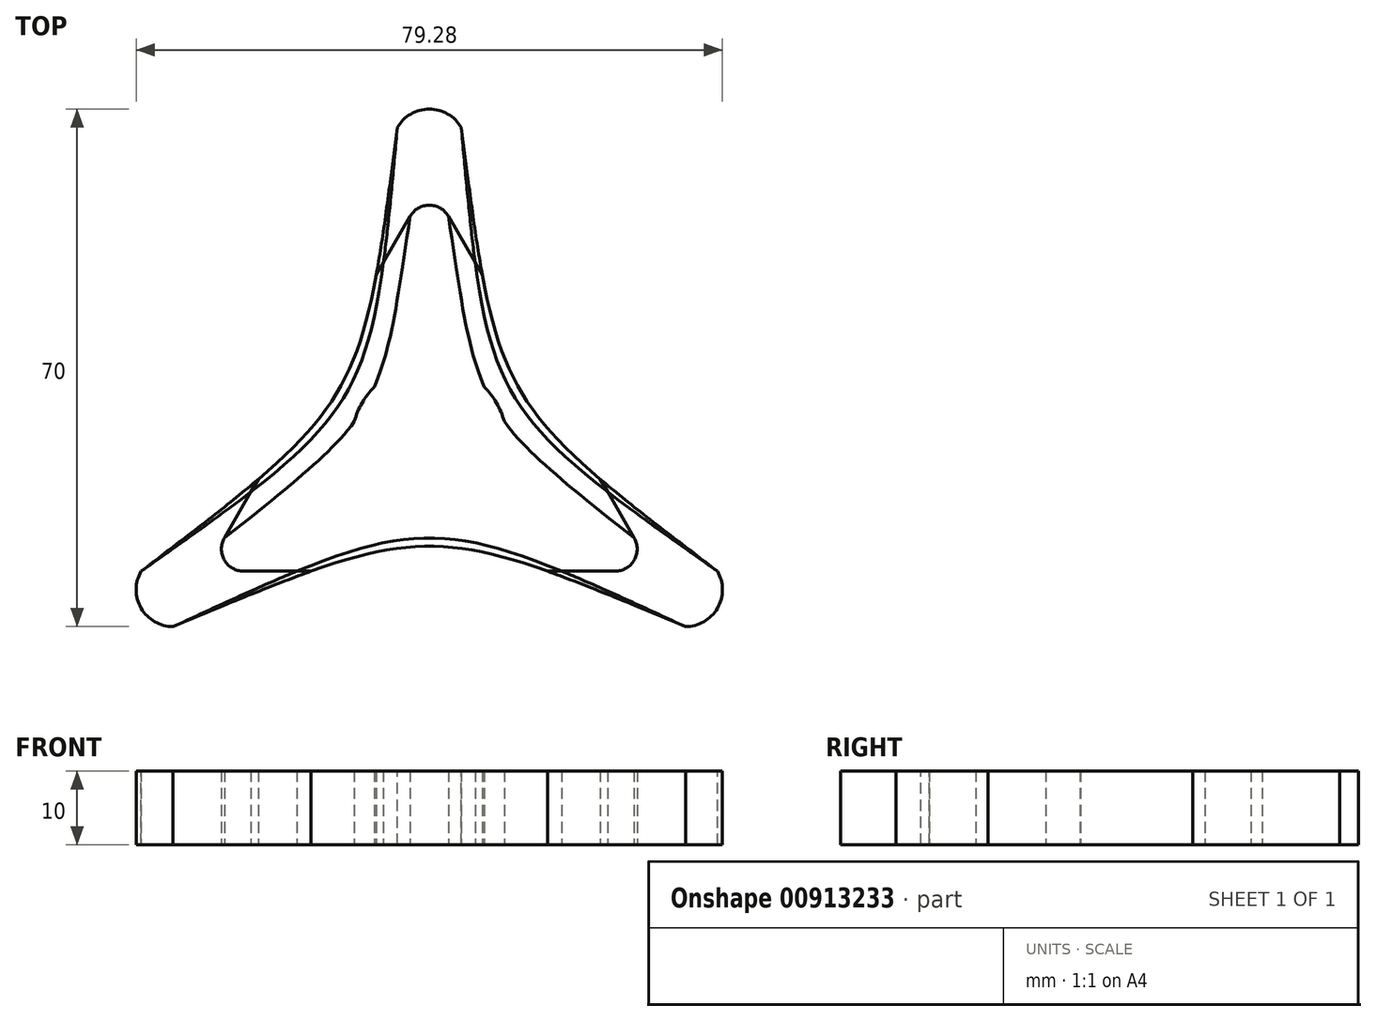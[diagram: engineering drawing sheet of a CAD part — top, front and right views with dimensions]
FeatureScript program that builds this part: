
annotation { "Feature Type Name" : "Feature", "Feature Type Description" : "" }
export const myFeature = defineFeature(function(context is Context, id is Id, definition is map)
    precondition{}
    {
        {
            var Q0;
            Q0=qCreatedBy(makeId("Top.planeOp"),FACE);
            var sketch = newSketch(context, id + "F0", { "sketchPlane" : qUnion([Q0])});
            skCircle(sketch, "E0", {"center": v(0, 0) * mm, "radius": 10.5 * mm});
            skCircle(sketch, "E1", {"center": v(0, 0) * mm, "radius": 50 * mm});
            skCircle(sketch, "E2", {"center": v(0, 0) * mm, "radius": 35 * mm});
            skCircle(sketch, "E3", {"center": v(0, 0) * mm, "radius": 7.5 * mm});
            skCircle(sketch, "E4.cCircle", {"center": v(0, 0) * mm, "radius": 7.5 * mm, "construction": true});
            skLineSegment(sketch, "E4.0", {"start": v(0, -7.5) * mm, "end": v(-6.5, 3.75) * mm});
            skLineSegment(sketch, "E4.1", {"start": v(-6.5, 3.75) * mm, "end": v(6.5, 3.75) * mm});
            skLineSegment(sketch, "E4.2", {"start": v(6.5, 3.75) * mm, "end": v(0, -7.5) * mm});
            skCircle(sketch, "E5.cCircle", {"center": v(0, 0) * mm, "radius": 10.5 * mm, "construction": true});
            skLineSegment(sketch, "E5.0", {"start": v(0, -10.5) * mm, "end": v(-9.1, 5.25) * mm});
            skLineSegment(sketch, "E5.1", {"start": v(-9.1, 5.25) * mm, "end": v(9.1, 5.25) * mm});
            skLineSegment(sketch, "E5.2", {"start": v(9.1, 5.25) * mm, "end": v(0, -10.5) * mm});
            skCircle(sketch, "E6.cCircle", {"center": v(0, 0) * mm, "radius": 35 * mm, "construction": true});
            skLineSegment(sketch, "E6.0", {"start": v(2.6, 30.5) * mm, "end": v(27.71, -13) * mm});
            skLineSegment(sketch, "E6.1", {"start": v(25.11, -17.5) * mm, "end": v(-25.11, -17.5) * mm});
            skLineSegment(sketch, "E6.2", {"start": v(-27.71, -13) * mm, "end": v(-2.6, 30.5) * mm});
            skCircle(sketch, "E7.cCircle", {"center": v(0, 0) * mm, "radius": 50 * mm, "construction": true});
            skLineSegment(sketch, "E7.0", {"start": v(4.33, 42.5) * mm, "end": v(38.97, -17.5) * mm});
            skLineSegment(sketch, "E7.1", {"start": v(34.64, -25) * mm, "end": v(-34.64, -25) * mm});
            skLineSegment(sketch, "E7.2", {"start": v(-38.97, -17.5) * mm, "end": v(-4.33, 42.5) * mm});
            skPoint(sketch, "E8.visualSharp", {"position": v(0, 50) * mm});
            skArc(sketch, "E8.filletArc", {"start": v(4.33, 42.5) * mm, "mid": v(0, 45) * mm, "end": v(-4.33, 42.5) * mm});
            skPoint(sketch, "E9.visualSharp", {"position": v(43.3, -25) * mm});
            skArc(sketch, "E9.filletArc", {"start": v(34.64, -25) * mm, "mid": v(38.97, -22.5) * mm, "end": v(38.97, -17.5) * mm});
            skPoint(sketch, "E10.visualSharp", {"position": v(-43.3, -25) * mm});
            skArc(sketch, "E10.filletArc", {"start": v(-38.97, -17.5) * mm, "mid": v(-38.97, -22.5) * mm, "end": v(-34.64, -25) * mm});
            skPoint(sketch, "E11.visualSharp", {"position": v(0, 35) * mm});
            skArc(sketch, "E11.filletArc", {"start": v(2.6, 30.5) * mm, "mid": v(0, 32) * mm, "end": v(-2.6, 30.5) * mm});
            skPoint(sketch, "E12.visualSharp", {"position": v(30.31, -17.5) * mm});
            skArc(sketch, "E12.filletArc", {"start": v(25.11, -17.5) * mm, "mid": v(27.71, -16) * mm, "end": v(27.71, -13) * mm});
            skPoint(sketch, "E13.visualSharp", {"position": v(-30.31, -17.5) * mm});
            skArc(sketch, "E13.filletArc", {"start": v(-27.71, -13) * mm, "mid": v(-27.71, -16) * mm, "end": v(-25.11, -17.5) * mm});
            skFitSpline(sketch, "E14", {"points": [v(4.33, 42.5) * mm, v(38.97, -17.5) * mm], "startDerivative": vector(14.29, -111.75) * mm, "endDerivative": vector(89.63, -68.25) * mm});
            skFitSpline(sketch, "E15", {"points": [v(27.71, -13) * mm, v(2.6, 30.5) * mm], "startDerivative": vector(-63.65, 50.25) * mm, "endDerivative": vector(-11.7, 80.25) * mm});
            skFitSpline(sketch, "E16", {"points": [v(-2.6, 30.5) * mm, v(-27.71, -13) * mm], "startDerivative": vector(-11.7, -80.25) * mm, "endDerivative": vector(-63.65, -50.25) * mm});
            skFitSpline(sketch, "E17", {"points": [v(-4.33, 42.5) * mm, v(-38.97, -17.5) * mm], "startDerivative": vector(-14.29, -111.75) * mm, "endDerivative": vector(-89.63, -68.25) * mm});
            skFitSpline(sketch, "E18", {"points": [v(-25.11, -17.5) * mm, v(25.11, -17.5) * mm], "startDerivative": vector(75.34, 30) * mm, "endDerivative": vector(75.34, -30) * mm});
            skFitSpline(sketch, "E19", {"points": [v(34.64, -25) * mm, v(-34.64, -25) * mm], "startDerivative": vector(-103.92, 43.5) * mm, "endDerivative": vector(-103.92, -43.5) * mm});
            skCircle(sketch, "E20", {"center": v(0, 0) * mm, "radius": 9 * mm});
            skLineSegment(sketch, "E21", {"start": v(-25.11, -17.5) * mm, "end": v(25.11, -17.5) * mm});
            skFitSpline(sketch, "E22", {"points": [v(-34.64, -25) * mm, v(34.64, -25) * mm], "startDerivative": vector(103.92, 48) * mm, "endDerivative": vector(103.92, -48) * mm});
            skFitSpline(sketch, "E23", {"points": [v(4.33, 42.5) * mm, v(38.97, -17.5) * mm], "startDerivative": vector(10.4, -114) * mm, "endDerivative": vector(93.53, -66) * mm});
            skFitSpline(sketch, "E24", {"points": [v(-4.33, 42.5) * mm, v(-38.97, -17.5) * mm], "startDerivative": vector(-10.4, -114) * mm, "endDerivative": vector(-93.53, -66) * mm});
            skCircle(sketch, "E25.cCircle", {"center": v(0, 0) * mm, "radius": 9 * mm, "construction": true});
            skLineSegment(sketch, "E25.0", {"start": v(0, -9) * mm, "end": v(-7.8, 4.5) * mm});
            skLineSegment(sketch, "E25.1", {"start": v(-7.8, 4.5) * mm, "end": v(7.8, 4.5) * mm});
            skLineSegment(sketch, "E25.2", {"start": v(7.8, 4.5) * mm, "end": v(0, -9) * mm});
            skSolve(sketch);
        }
        {
            var Q0;
            {var subQ1=sQuery(id+"F0.wireOp",EDGE,"E6.1");var subQ3=sQuery(id+"F0.wireOp",EDGE,"E19");var subQ6=makeQuery(id+"F0.imprint","INTERSECT",VERTEX,{"disambiguationData":[OD(0.0)],"derivedFrom":[subQ1,subQ3]});Q0=makeQuery(id+"F0.imprint","IMPRINT",FACE,{"disambiguationData":[TD([[makeQuery(id+"F0.imprint","IMPRINT",EDGE,{"disambiguationData":[TD([[subQ6,-1.0]])],"derivedFrom":subQ3}),-1.0]])]});}
            var Q1;
            {var subQ0=sQuery(id+"F0.wireOp",EDGE,"E12.filletArc");Q1=makeQuery(id+"F0.imprint","IMPRINT",FACE,{"disambiguationData":[TD([[makeQuery(id+"F0.imprint","IMPRINT",EDGE,{"derivedFrom":subQ0}),-1.0]])]});}
            var Q2;
            {var subQ5=sQuery(id+"F0.wireOp",EDGE,"E9.filletArc");Q2=makeQuery(id+"F0.imprint","IMPRINT",FACE,{"disambiguationData":[TD([[makeQuery(id+"F0.imprint","IMPRINT",EDGE,{"derivedFrom":subQ5}),1.0]])]});}
            var Q3;
            {var subQ1=sQuery(id+"F0.wireOp",EDGE,"E6.0");var subQ3=sQuery(id+"F0.wireOp",EDGE,"E14");var subQ4=makeQuery(id+"F0.imprint","INTERSECT",VERTEX,{"disambiguationData":[OD(0.0)],"derivedFrom":[subQ1,subQ3]});Q3=makeQuery(id+"F0.imprint","IMPRINT",FACE,{"disambiguationData":[TD([[makeQuery(id+"F0.imprint","IMPRINT",EDGE,{"disambiguationData":[TD([[subQ4,-1.0]])],"derivedFrom":subQ3}),-1.0]])]});}
            var Q4;
            {var subQ0=sQuery(id+"F0.wireOp",EDGE,"E13.filletArc");Q4=makeQuery(id+"F0.imprint","IMPRINT",FACE,{"disambiguationData":[TD([[makeQuery(id+"F0.imprint","IMPRINT",EDGE,{"derivedFrom":subQ0}),-1.0]])]});}
            var Q5;
            {var subQ5=sQuery(id+"F0.wireOp",EDGE,"E10.filletArc");Q5=makeQuery(id+"F0.imprint","IMPRINT",FACE,{"disambiguationData":[TD([[makeQuery(id+"F0.imprint","IMPRINT",EDGE,{"derivedFrom":subQ5}),1.0]])]});}
            var Q6;
            {var subQ1=sQuery(id+"F0.wireOp",EDGE,"E6.2");var subQ3=sQuery(id+"F0.wireOp",EDGE,"E17");var subQ5=makeQuery(id+"F0.imprint","INTERSECT",VERTEX,{"disambiguationData":[OD(0.0)],"derivedFrom":[subQ1,subQ3]});Q6=makeQuery(id+"F0.imprint","IMPRINT",FACE,{"disambiguationData":[TD([[makeQuery(id+"F0.imprint","IMPRINT",EDGE,{"disambiguationData":[TD([[subQ5,1.0]])],"derivedFrom":subQ3}),1.0]])]});}
            var Q7;
            {var subQ5=sQuery(id+"F0.wireOp",EDGE,"E8.filletArc");Q7=makeQuery(id+"F0.imprint","IMPRINT",FACE,{"disambiguationData":[TD([[makeQuery(id+"F0.imprint","IMPRINT",EDGE,{"derivedFrom":subQ5}),1.0]])]});}
            var Q8;
            {var subQ0=sQuery(id+"F0.wireOp",EDGE,"E11.filletArc");Q8=makeQuery(id+"F0.imprint","IMPRINT",FACE,{"disambiguationData":[TD([[makeQuery(id+"F0.imprint","IMPRINT",EDGE,{"derivedFrom":subQ0}),-1.0]])]});}
            extrude(context, id + "F1", {"entities" : qUnion([Q0, Q1, Q2, Q3, Q4, Q5, Q6, Q7, Q8]), "depth" : 10 * mm, "offsetDistance" : 25 * mm});
        }
        {
            var Q0;
            {var subQ5=sQuery(id+"F0.wireOp",EDGE,"E10.filletArc");Q0=makeQuery(id+"F0.imprint","IMPRINT",FACE,{"disambiguationData":[TD([[makeQuery(id+"F0.imprint","IMPRINT",EDGE,{"derivedFrom":subQ5}),1.0]])]});}
            var Q1;
            {var subQ1=sQuery(id+"F0.wireOp",EDGE,"E13.filletArc");Q1=makeQuery(id+"F0.imprint","IMPRINT",FACE,{"disambiguationData":[TD([[makeQuery(id+"F0.imprint","IMPRINT",EDGE,{"derivedFrom":subQ1}),-1.0]])]});}
            var Q2;
            {var subQ0=sQuery(id+"F0.wireOp",EDGE,"E21");var subQ8=sQuery(id+"F0.wireOp",EDGE,"E22");var subQ9=makeQuery(id+"F0.imprint","INTERSECT",VERTEX,{"disambiguationData":[OD(0.0)],"derivedFrom":[subQ0,subQ8]});Q2=makeQuery(id+"F0.imprint","IMPRINT",FACE,{"disambiguationData":[TD([[makeQuery(id+"F0.imprint","IMPRINT",EDGE,{"disambiguationData":[TD([[subQ9,-1.0]])],"derivedFrom":subQ8}),1.0]])]});}
            var Q3;
            {var subQ1=sQuery(id+"F0.wireOp",EDGE,"E6.2");var subQ3=sQuery(id+"F0.wireOp",EDGE,"E24");var subQ6=makeQuery(id+"F0.imprint","INTERSECT",VERTEX,{"disambiguationData":[OD(0.0)],"derivedFrom":[subQ1,subQ3]});Q3=makeQuery(id+"F0.imprint","IMPRINT",FACE,{"disambiguationData":[TD([[makeQuery(id+"F0.imprint","IMPRINT",EDGE,{"disambiguationData":[TD([[subQ6,1.0]])],"derivedFrom":subQ3}),1.0]])]});}
            var Q4;
            {var subQ0=sQuery(id+"F0.wireOp",EDGE,"E17");var subQ1=sQuery(id+"F0.wireOp",EDGE,"E2");var subQ2=makeQuery(id+"F0.imprint","INTERSECT",VERTEX,{"disambiguationData":[OD(1.0)],"derivedFrom":[subQ1,subQ0]});Q4=makeQuery(id+"F0.imprint","IMPRINT",FACE,{"disambiguationData":[TD([[makeQuery(id+"F0.imprint","IMPRINT",EDGE,{"disambiguationData":[TD([[subQ2,-1.0]])],"derivedFrom":subQ1}),1.0]])]});}
            var Q5;
            {var subQ0=sQuery(id+"F0.wireOp",EDGE,"E17");var subQ1=sQuery(id+"F0.wireOp",EDGE,"E2");var subQ2=makeQuery(id+"F0.imprint","INTERSECT",VERTEX,{"disambiguationData":[OD(1.0)],"derivedFrom":[subQ1,subQ0]});Q5=makeQuery(id+"F0.imprint","IMPRINT",FACE,{"disambiguationData":[TD([[makeQuery(id+"F0.imprint","IMPRINT",EDGE,{"disambiguationData":[TD([[subQ2,-1.0]])],"derivedFrom":subQ1}),-1.0]])]});}
            var Q6;
            {var subQ0=sQuery(id+"F0.wireOp",EDGE,"E22");var subQ1=sQuery(id+"F0.wireOp",EDGE,"E2");var subQ2=makeQuery(id+"F0.imprint","INTERSECT",VERTEX,{"disambiguationData":[OD(0.0)],"derivedFrom":[subQ1,subQ0]});Q6=makeQuery(id+"F0.imprint","IMPRINT",FACE,{"disambiguationData":[TD([[makeQuery(id+"F0.imprint","IMPRINT",EDGE,{"disambiguationData":[TD([[subQ2,-1.0]])],"derivedFrom":subQ1}),-1.0]])]});}
            var Q7;
            {var subQ0=sQuery(id+"F0.wireOp",EDGE,"E22");var subQ1=sQuery(id+"F0.wireOp",EDGE,"E2");var subQ2=makeQuery(id+"F0.imprint","INTERSECT",VERTEX,{"disambiguationData":[OD(0.0)],"derivedFrom":[subQ1,subQ0]});Q7=makeQuery(id+"F0.imprint","IMPRINT",FACE,{"disambiguationData":[TD([[makeQuery(id+"F0.imprint","IMPRINT",EDGE,{"disambiguationData":[TD([[subQ2,-1.0]])],"derivedFrom":subQ1}),1.0]])]});}
            var Q8;
            {var subQ0=sQuery(id+"F0.wireOp",EDGE,"E21");var subQ1=sQuery(id+"F0.wireOp",EDGE,"E19");var subQ2=makeQuery(id+"F0.imprint","INTERSECT",VERTEX,{"disambiguationData":[OD(0.0)],"derivedFrom":[subQ1,subQ0]});Q8=makeQuery(id+"F0.imprint","IMPRINT",FACE,{"disambiguationData":[TD([[makeQuery(id+"F0.imprint","IMPRINT",EDGE,{"disambiguationData":[TD([[subQ2,-1.0]])],"derivedFrom":subQ1}),-1.0]])]});}
            var Q9;
            {var subQ1=sQuery(id+"F0.wireOp",EDGE,"E12.filletArc");Q9=makeQuery(id+"F0.imprint","IMPRINT",FACE,{"disambiguationData":[TD([[makeQuery(id+"F0.imprint","IMPRINT",EDGE,{"derivedFrom":subQ1}),-1.0]])]});}
            var Q10;
            {var subQ1=sQuery(id+"F0.wireOp",EDGE,"E6.0");var subQ3=sQuery(id+"F0.wireOp",EDGE,"E23");var subQ4=makeQuery(id+"F0.imprint","INTERSECT",VERTEX,{"disambiguationData":[OD(0.0)],"derivedFrom":[subQ1,subQ3]});Q10=makeQuery(id+"F0.imprint","IMPRINT",FACE,{"disambiguationData":[TD([[makeQuery(id+"F0.imprint","IMPRINT",EDGE,{"disambiguationData":[TD([[subQ4,-1.0]])],"derivedFrom":subQ3}),-1.0]])]});}
            var Q11;
            {var subQ5=sQuery(id+"F0.wireOp",EDGE,"E9.filletArc");Q11=makeQuery(id+"F0.imprint","IMPRINT",FACE,{"disambiguationData":[TD([[makeQuery(id+"F0.imprint","IMPRINT",EDGE,{"derivedFrom":subQ5}),1.0]])]});}
            var Q12;
            {var subQ0=sQuery(id+"F0.wireOp",EDGE,"E19");var subQ1=sQuery(id+"F0.wireOp",EDGE,"E2");var subQ2=makeQuery(id+"F0.imprint","INTERSECT",VERTEX,{"disambiguationData":[OD(1.0)],"derivedFrom":[subQ1,subQ0]});Q12=makeQuery(id+"F0.imprint","IMPRINT",FACE,{"disambiguationData":[TD([[makeQuery(id+"F0.imprint","IMPRINT",EDGE,{"disambiguationData":[TD([[subQ2,-1.0]])],"derivedFrom":subQ1}),-1.0]])]});}
            var Q13;
            {var subQ0=sQuery(id+"F0.wireOp",EDGE,"E19");var subQ1=sQuery(id+"F0.wireOp",EDGE,"E2");var subQ2=makeQuery(id+"F0.imprint","INTERSECT",VERTEX,{"disambiguationData":[OD(1.0)],"derivedFrom":[subQ1,subQ0]});Q13=makeQuery(id+"F0.imprint","IMPRINT",FACE,{"disambiguationData":[TD([[makeQuery(id+"F0.imprint","IMPRINT",EDGE,{"disambiguationData":[TD([[subQ2,-1.0]])],"derivedFrom":subQ1}),1.0]])]});}
            var Q14;
            {var subQ0=sQuery(id+"F0.wireOp",EDGE,"E23");var subQ1=sQuery(id+"F0.wireOp",EDGE,"E2");var subQ2=makeQuery(id+"F0.imprint","INTERSECT",VERTEX,{"disambiguationData":[OD(1.0)],"derivedFrom":[subQ1,subQ0]});Q14=makeQuery(id+"F0.imprint","IMPRINT",FACE,{"disambiguationData":[TD([[makeQuery(id+"F0.imprint","IMPRINT",EDGE,{"disambiguationData":[TD([[subQ2,-1.0]])],"derivedFrom":subQ1}),-1.0]])]});}
            var Q15;
            {var subQ0=sQuery(id+"F0.wireOp",EDGE,"E23");var subQ1=sQuery(id+"F0.wireOp",EDGE,"E2");var subQ2=makeQuery(id+"F0.imprint","INTERSECT",VERTEX,{"disambiguationData":[OD(1.0)],"derivedFrom":[subQ1,subQ0]});Q15=makeQuery(id+"F0.imprint","IMPRINT",FACE,{"disambiguationData":[TD([[makeQuery(id+"F0.imprint","IMPRINT",EDGE,{"disambiguationData":[TD([[subQ2,-1.0]])],"derivedFrom":subQ1}),1.0]])]});}
            var Q16;
            {var subQ0=sQuery(id+"F0.wireOp",EDGE,"E23");var subQ1=sQuery(id+"F0.wireOp",EDGE,"E6.0");var subQ2=makeQuery(id+"F0.imprint","INTERSECT",VERTEX,{"disambiguationData":[OD(0.0)],"derivedFrom":[subQ1,subQ0]});Q16=makeQuery(id+"F0.imprint","IMPRINT",FACE,{"disambiguationData":[TD([[makeQuery(id+"F0.imprint","IMPRINT",EDGE,{"disambiguationData":[TD([[subQ2,-1.0]])],"derivedFrom":subQ1}),-1.0]])]});}
            var Q17;
            {var subQ5=sQuery(id+"F0.wireOp",EDGE,"E8.filletArc");Q17=makeQuery(id+"F0.imprint","IMPRINT",FACE,{"disambiguationData":[TD([[makeQuery(id+"F0.imprint","IMPRINT",EDGE,{"derivedFrom":subQ5}),1.0]])]});}
            var Q18;
            {var subQ0=sQuery(id+"F0.wireOp",EDGE,"E11.filletArc");Q18=makeQuery(id+"F0.imprint","IMPRINT",FACE,{"disambiguationData":[TD([[makeQuery(id+"F0.imprint","IMPRINT",EDGE,{"derivedFrom":subQ0}),-1.0]])]});}
            var Q19;
            {var subQ0=sQuery(id+"F0.wireOp",EDGE,"E14");var subQ1=sQuery(id+"F0.wireOp",EDGE,"E2");var subQ2=makeQuery(id+"F0.imprint","INTERSECT",VERTEX,{"disambiguationData":[OD(0.0)],"derivedFrom":[subQ1,subQ0]});Q19=makeQuery(id+"F0.imprint","IMPRINT",FACE,{"disambiguationData":[TD([[makeQuery(id+"F0.imprint","IMPRINT",EDGE,{"disambiguationData":[TD([[subQ2,-1.0]])],"derivedFrom":subQ1}),1.0]])]});}
            var Q20;
            {var subQ0=sQuery(id+"F0.wireOp",EDGE,"E14");var subQ1=sQuery(id+"F0.wireOp",EDGE,"E2");var subQ2=makeQuery(id+"F0.imprint","INTERSECT",VERTEX,{"disambiguationData":[OD(0.0)],"derivedFrom":[subQ1,subQ0]});Q20=makeQuery(id+"F0.imprint","IMPRINT",FACE,{"disambiguationData":[TD([[makeQuery(id+"F0.imprint","IMPRINT",EDGE,{"disambiguationData":[TD([[subQ2,-1.0]])],"derivedFrom":subQ1}),-1.0]])]});}
            var Q21;
            {var subQ0=sQuery(id+"F0.wireOp",EDGE,"E24");var subQ1=sQuery(id+"F0.wireOp",EDGE,"E2");var subQ2=makeQuery(id+"F0.imprint","INTERSECT",VERTEX,{"disambiguationData":[OD(0.0)],"derivedFrom":[subQ1,subQ0]});Q21=makeQuery(id+"F0.imprint","IMPRINT",FACE,{"disambiguationData":[TD([[makeQuery(id+"F0.imprint","IMPRINT",EDGE,{"disambiguationData":[TD([[subQ2,-1.0]])],"derivedFrom":subQ1}),1.0]])]});}
            var Q22;
            {var subQ0=sQuery(id+"F0.wireOp",EDGE,"E24");var subQ1=sQuery(id+"F0.wireOp",EDGE,"E2");var subQ2=makeQuery(id+"F0.imprint","INTERSECT",VERTEX,{"disambiguationData":[OD(0.0)],"derivedFrom":[subQ1,subQ0]});Q22=makeQuery(id+"F0.imprint","IMPRINT",FACE,{"disambiguationData":[TD([[makeQuery(id+"F0.imprint","IMPRINT",EDGE,{"disambiguationData":[TD([[subQ2,-1.0]])],"derivedFrom":subQ1}),-1.0]])]});}
            var Q23;
            {var subQ0=sQuery(id+"F0.wireOp",EDGE,"E24");var subQ1=sQuery(id+"F0.wireOp",EDGE,"E6.2");var subQ2=makeQuery(id+"F0.imprint","INTERSECT",VERTEX,{"disambiguationData":[OD(0.0)],"derivedFrom":[subQ1,subQ0]});Q23=makeQuery(id+"F0.imprint","IMPRINT",FACE,{"disambiguationData":[TD([[makeQuery(id+"F0.imprint","IMPRINT",EDGE,{"disambiguationData":[TD([[subQ2,-1.0]])],"derivedFrom":subQ1}),-1.0]])]});}
            extrude(context, id + "F2", {"entities" : qUnion([Q0, Q1, Q2, Q3, Q4, Q5, Q6, Q7, Q8, Q9, Q10, Q11, Q12, Q13, Q14, Q15, Q16, Q17, Q18, Q19, Q20, Q21, Q22, Q23]), "depth" : 10 * mm, "offsetDistance" : 25 * mm});
        }
    });
